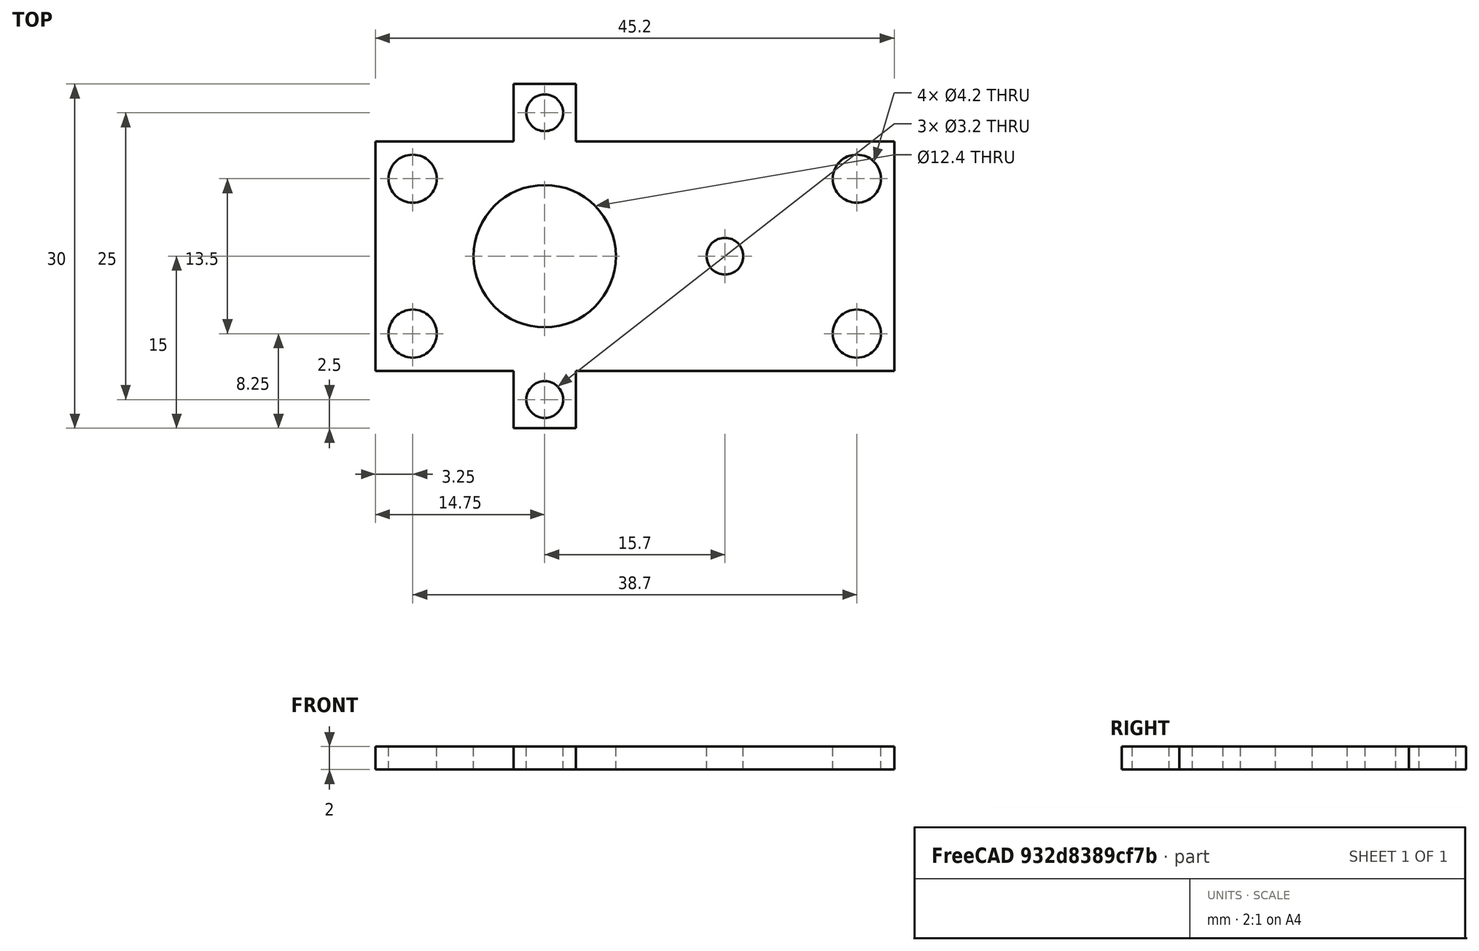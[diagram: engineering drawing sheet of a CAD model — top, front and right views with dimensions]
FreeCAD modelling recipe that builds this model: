
FCSTD DOCUMENT  (FreeCAD 0.17R13522 (Git))
Label: v5_base_superior
License: CreativeCommons Attribution-ShareAlike
LicenseURL: http://creativecommons.org/licenses/by-sa/4.0/
objects: Part::Cut×9, Part::Cylinder×8, Part::Box×3, Part::Fuse×2
note: 22 computed .brp shape members not serialized (recipe doc carries the construction recipe); baked Part::Feature solids carry a one-line shape summary decoded from their .brp

FEATURE [Part::Box] Box  label="base"
  AttacherType = Attacher::AttachEngine3D
  Height = 2
  Length = 45.2
  Width = 20
FEATURE [Part::Cylinder] Cylinder
  Angle = 360
  AttacherType = Attacher::AttachEngine3D
  Height = 10
  Placement = pos=(41.95,16.75,-5) rot=(0,0,1;0rad)
  Radius = 2.1
FEATURE [Part::Cylinder] Cylinder001
  Angle = 360
  AttacherType = Attacher::AttachEngine3D
  Height = 10
  Placement = pos=(41.95,3.25,-5) rot=(0,0,1;0rad)
  Radius = 2.1
FEATURE [Part::Cylinder] Cylinder002
  Angle = 360
  AttacherType = Attacher::AttachEngine3D
  Height = 10
  Placement = pos=(3.25,16.75,-5) rot=(0,0,1;0rad)
  Radius = 2.1
FEATURE [Part::Cylinder] Cylinder003
  Angle = 360
  AttacherType = Attacher::AttachEngine3D
  Height = 10
  Placement = pos=(3.25,3.25,-5) rot=(0,0,1;0rad)
  Radius = 2.1
FEATURE [Part::Cut] Cut
  Base = -> Box
  Refine = true
  Tool = -> Cylinder003
FEATURE [Part::Cut] Cut001
  Base = -> Cut
  Refine = true
  Tool = -> Cylinder002
FEATURE [Part::Cut] Cut002
  Base = -> Cut001
  Refine = true
  Tool = -> Cylinder
FEATURE [Part::Cut] Cut003
  Base = -> Cut002
  Refine = true
  Tool = -> Cylinder001
FEATURE [Part::Cylinder] Cylinder004
  Angle = 360
  AttacherType = Attacher::AttachEngine3D
  Height = 10
  Placement = pos=(14.75,10,-4) rot=(0,0,1;0rad)
  Radius = 6.2
FEATURE [Part::Cylinder] Cylinder005
  Angle = 360
  AttacherType = Attacher::AttachEngine3D
  Height = 10
  Placement = pos=(30.45,10,-5) rot=(0,0,1;0rad)
  Radius = 1.6
FEATURE [Part::Cut] Cut004
  Base = -> Cut003
  Refine = true
  Tool = -> Cylinder004
FEATURE [Part::Cut] Cut005
  Base = -> Cut004
  Refine = true
  Tool = -> Cylinder005
FEATURE [Part::Cylinder] Cylinder006
  Angle = 360
  AttacherType = Attacher::AttachEngine3D
  Height = 10
  Placement = pos=(14.75,22.5,-4) rot=(0,0,1;0rad)
  Radius = 1.6
FEATURE [Part::Cylinder] Cylinder007
  Angle = 360
  AttacherType = Attacher::AttachEngine3D
  Height = 10
  Placement = pos=(14.75,-2.5,-4) rot=(0,0,1;0rad)
  Radius = 1.6
FEATURE [Part::Box] Box001  label="Cube"
  AttacherType = Attacher::AttachEngine3D
  Height = 2
  Length = 5.4
  Placement = pos=(12.05,-5,0) rot=(0,0,1;0rad)
  Width = 5
FEATURE [Part::Box] Box002  label="Cube001"
  AttacherType = Attacher::AttachEngine3D
  Height = 2
  Length = 5.4
  Placement = pos=(12.05,20,0) rot=(0,0,1;0rad)
  Width = 5
FEATURE [Part::Fuse] Fusion
  Base = -> Cut005
  Refine = true
  Tool = -> Box002
FEATURE [Part::Fuse] Fusion001
  Base = -> Box001
  Refine = true
  Tool = -> Fusion
FEATURE [Part::Cut] Cut006
  Base = -> Fusion001
  Refine = true
  Tool = -> Cylinder004
FEATURE [Part::Cut] Cut007
  Base = -> Cut006
  Refine = true
  Tool = -> Cylinder007
FEATURE [Part::Cut] Cut008
  Base = -> Cut007
  Refine = true
  Tool = -> Cylinder006
